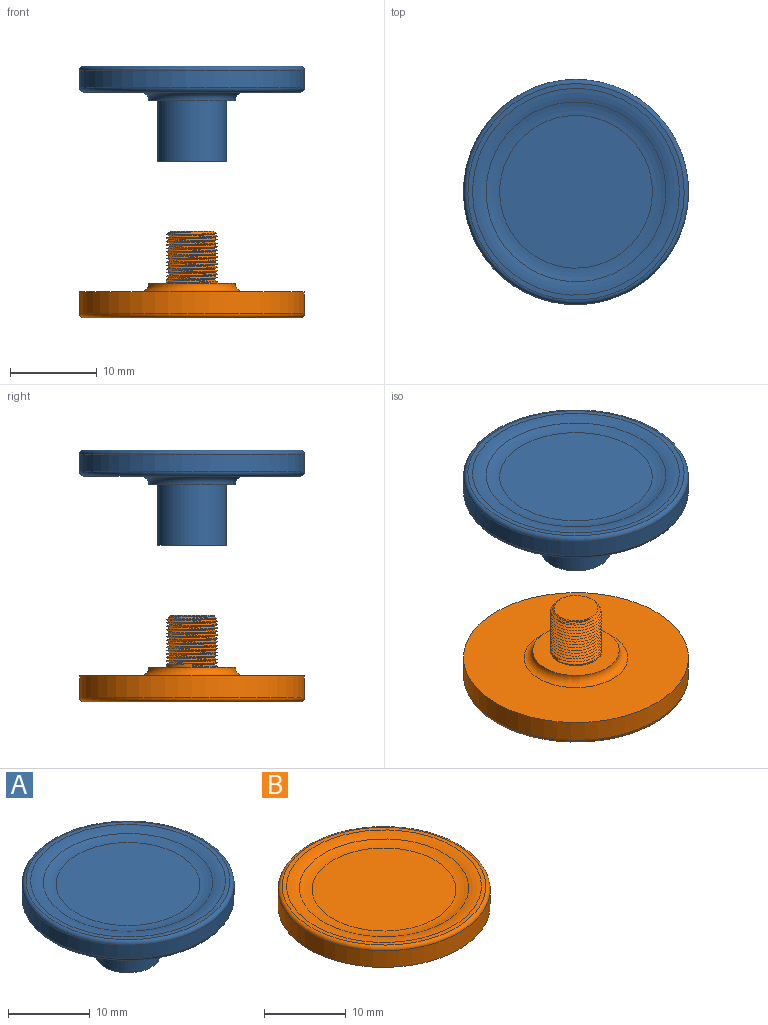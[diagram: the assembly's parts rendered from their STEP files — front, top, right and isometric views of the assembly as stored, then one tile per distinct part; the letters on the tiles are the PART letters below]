
ASSEMBLY  parts=2 mates=1
PART A: 21 faces, bbox 28.1x28.1x12.2 mm
  f0: cylinder r=3mm len=7.07mm, axis (0,0,1), area -10.2mm2, adj f14,f15,f18,f19
  f1: cylinder r=4mm len=8mm, axis (0,0,1), area 175.9mm2, adj f2,f4
  f2: plane 8x8mm, normal (0,0,-1), area 12.5mm2, adj f1,f16
  f3: plane 5.07x5.07mm, normal (0,0,-1), area 20.2mm2, adj f14
  f4: plane 10x10mm, normal (0,0,-1), area 28.3mm2, adj f1,f13
  f5: plane 25x25mm, normal (0,0,-1), area 377.8mm2, adj f11,f13
  f6: cylinder r=13mm len=26mm, axis (0,0,-1), area 163.4mm2, adj f11,f12
  f7: plane 25x25mm, normal (0,0,1), area 42.8mm2, adj f10,f12
  f8: plane 17.64x17.64mm, normal (0,0,1), area 244.4mm2, adj f9
  f9: torus R=8.82mm, axis (0,0,-1), area 95.9mm2, adj f8,f10
  f10: torus R=11.94mm, axis (0,0,1), area 111.3mm2, adj f7,f9
  f11: torus R=12.5mm, axis (0,0,1), area 63.3mm2, adj f5,f6
  f12: torus R=12.5mm, axis (0,0,1), area 63.3mm2, adj f6,f7
  f13: torus R=6mm, axis (0,0,1), area 52.9mm2, adj f4,f5
  f14: cone r=3mm half-angle=45deg, axis (0,0,-1), area 11.5mm2, adj f0,f3,f20
  f15: cone r=3.47mm half-angle=45deg, axis (0,0,-1), area 1.6mm2, adj f0,f16,f18,f19
  f16: cone r=3.47mm half-angle=45deg, axis (0,0,-1), area 6.9mm2, adj f2,f15,f19
  f17: plane 0.47x0.4mm, normal (0,-1,0), area 0.1mm2, adj f18,f19,f20
  f18: bspline ~7.94x6.81mm, area 134.8mm2, adj f0,f15,f17,f19,f20
  f19: bspline ~7.97x7.86mm, area 132.1mm2, adj f0,f15,f16,f17,f18
  f20: cylinder r=3mm len=6mm, axis (0,0,1), area 3.9mm2, adj f14,f17,f18
PART B: 17 faces, bbox 28.1x28.1x11.1 mm
  f0: cylinder r=3mm len=6mm, axis (0,0,1), area 3.8mm2, adj f3,f10,f13
  f1: cylinder r=13mm len=26mm, axis (0,0,-1), area 204.2mm2, adj f2,f8
  f2: plane 26x26mm, normal (0,0,-1), area 417.8mm2, adj f1,f9
  f3: plane 10x10mm, normal (0,0,-1), area 50.3mm2, adj f0,f9
  f4: plane 25x25mm, normal (0,0,1), area 42.8mm2, adj f7,f8
  f5: plane 17.64x17.64mm, normal (0,0,1), area 244.4mm2, adj f6
  f6: torus R=8.82mm, axis (0,0,-1), area 95.9mm2, adj f5,f7
  f7: torus R=11.94mm, axis (0,0,1), area 111.3mm2, adj f4,f6
  f8: torus R=12.5mm, axis (0,0,1), area 63.3mm2, adj f1,f4
  f9: torus R=6mm, axis (0,0,1), area 52.9mm2, adj f2,f3
  f10: plane 0.43x0.4mm, normal (0,-1,0), area 0.1mm2, adj f0,f11,f12,f13
  f11: bspline ~6.8x5.93mm, area 94.5mm2, adj f10,f12,f15,f16
  f12: bspline ~6.8x5.93mm, area 98.2mm2, adj f10,f11,f13,f15,f16
  f13: bspline ~6.93x6mm, area 1.2mm2, adj f0,f10,f12
  f14: plane 5.07x5.07mm, normal (0,0,-1), area 20.2mm2, adj f16
  f15: cone r=3mm half-angle=45deg, axis (0,0,1), area 0.1mm2, adj f11,f12,f16
  f16: cone r=3mm half-angle=45deg, axis (0,0,1), area 5.5mm2, adj f11,f12,f14,f15
PLACE A rot(axis=(0,0,-1),170.8deg) t=(-9.47,6.02,7.33)mm
PLACE B rot(axis=(0,1,0),180deg) t=(-9.47,6.02,-15.77)mm
MATE cylindrical B.f0 <-> A.f0  axis (0,0,1) through (-9.47,6.02,-8.77)mm
